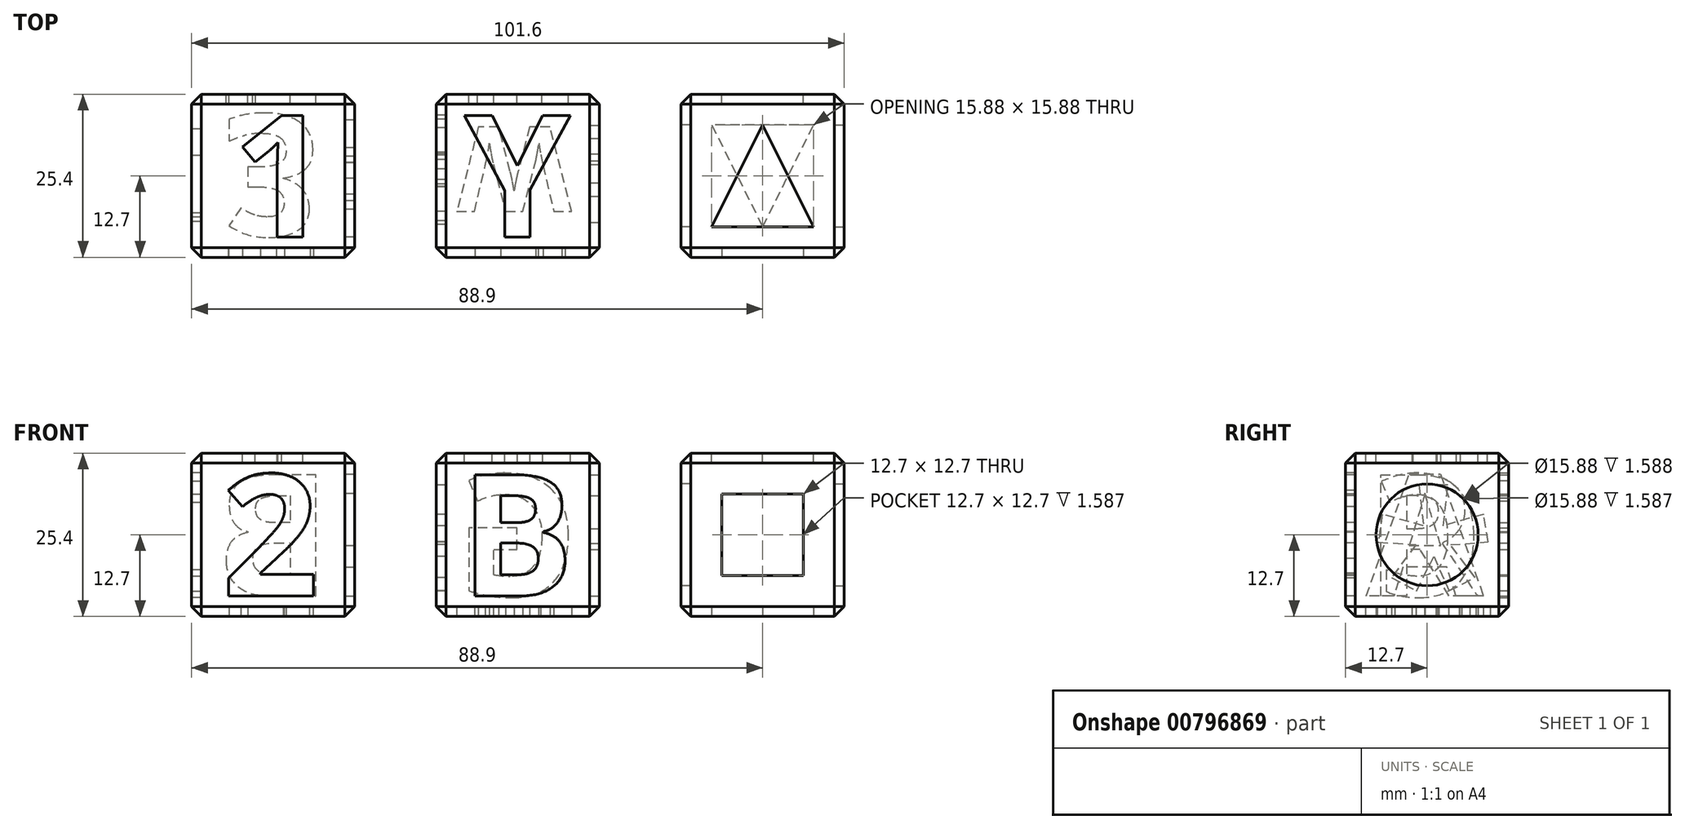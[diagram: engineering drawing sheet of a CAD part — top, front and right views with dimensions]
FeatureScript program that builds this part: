
annotation { "Feature Type Name" : "Feature", "Feature Type Description" : "" }
export const myFeature = defineFeature(function(context is Context, id is Id, definition is map)
    precondition{}
    {
        {
            var Q0;
            Q0=qCreatedBy(makeId("Top.planeOp"),FACE);
            var sketch = newSketch(context, id + "F0", { "sketchPlane" : qUnion([Q0])});
            skLineSegment(sketch, "E0.bottom", {"start": v(-12.7, 12.7) * mm, "end": v(12.7, 12.7) * mm});
            skLineSegment(sketch, "E0.top", {"start": v(-12.7, -12.7) * mm, "end": v(12.7, -12.7) * mm});
            skLineSegment(sketch, "E0.left", {"start": v(-12.7, 12.7) * mm, "end": v(-12.7, -12.7) * mm});
            skLineSegment(sketch, "E0.right", {"start": v(12.7, 12.7) * mm, "end": v(12.7, -12.7) * mm});
            skLineSegment(sketch, "E1.bottom", {"start": v(-50.8, 12.7) * mm, "end": v(-25.4, 12.7) * mm});
            skLineSegment(sketch, "E1.top", {"start": v(-50.8, -12.7) * mm, "end": v(-25.4, -12.7) * mm});
            skLineSegment(sketch, "E1.left", {"start": v(-50.8, 12.7) * mm, "end": v(-50.8, -12.7) * mm});
            skLineSegment(sketch, "E1.right", {"start": v(-25.4, 12.7) * mm, "end": v(-25.4, -12.7) * mm});
            skLineSegment(sketch, "E2.bottom", {"start": v(25.4, 12.7) * mm, "end": v(50.8, 12.7) * mm});
            skLineSegment(sketch, "E2.top", {"start": v(25.4, -12.7) * mm, "end": v(50.8, -12.7) * mm});
            skLineSegment(sketch, "E2.left", {"start": v(25.4, 12.7) * mm, "end": v(25.4, -12.7) * mm});
            skLineSegment(sketch, "E2.right", {"start": v(50.8, 12.7) * mm, "end": v(50.8, -12.7) * mm});
            skSolve(sketch);
        }
        {
            var Q0;
            Q0 = qSketchRegion(id + "F0", true);
            extrude(context, id + "F1", {"entities" : qUnion([Q0]), "depth" : 25.4 * mm, "offsetDistance" : 25.4 * mm});
        }
        {
            var Q0;
            Q0=makeQuery(id+"F1.opExtrude","CAP_FACE",FACE,{"disambiguationData":[OSD([sQuery(id+"F0.wireOp",EDGE,"E1.bottom"),sQuery(id+"F0.wireOp",EDGE,"E1.top"),sQuery(id+"F0.wireOp",EDGE,"E1.left"),sQuery(id+"F0.wireOp",EDGE,"E1.right")])],"isStart":false});
            var sketch = newSketch(context, id + "F2", { "sketchPlane" : qUnion([Q0])});
            skText(sketch, "E3", { "text": "1", "fontName": "OpenSans-Bold.ttf"});
            const initialGuessF2  = {"E3": [-0.04442, -0.00952, 1, 0, 0.01905]};
            skSetInitialGuess(sketch, initialGuessF2);
            skSolve(sketch);
        }
        {
            var Q0;
            Q0 = qSketchRegion(id + "F2", true);
            extrude(context, id + "F3", {"entities" : qUnion([Q0]), "operationType" : NewBodyOperationType.REMOVE, "oppositeDirection" : true, "depth" : 1.59 * mm, "offsetDistance" : 25.4 * mm});
        }
        {
            var Q0;
            Q0=makeQuery(id+"F1.opExtrude","SWEPT_FACE",FACE,{"disambiguationData":[OSD([sQuery(id+"F0.wireOp",EDGE,"E1.top")])]});
            var sketch = newSketch(context, id + "F4", { "sketchPlane" : qUnion([Q0])});
            skText(sketch, "E4", { "text": "2", "fontName": "OpenSans-Bold.ttf"});
            skPoint(sketch, "E4.firstSnap0", {"position": v(-38.1, 25.4) * mm});
            const initialGuessF4  = {"E4": [-0.04609, 0.00318, 1, 0, 0.01905]};
            skSetInitialGuess(sketch, initialGuessF4);
            skSolve(sketch);
        }
        {
            var Q0;
            Q0=makeQuery(id+"F4.imprint","IMPRINT",FACE,{"disambiguationData":[TD([[makeQuery(id+"F4.imprint","IMPRINT",EDGE,{"derivedFrom":sQuery(id+"F4.wireOp",EDGE,"E4.sketch_text.stroke-0")}),-1.0]])]});
            extrude(context, id + "F5", {"entities" : qUnion([Q0]), "operationType" : NewBodyOperationType.REMOVE, "oppositeDirection" : true, "depth" : 1.59 * mm, "offsetDistance" : 25.4 * mm});
        }
        {
            var Q0;
            Q0=makeQuery(id+"F1.opExtrude","CAP_FACE",FACE,{"disambiguationData":[OSD([sQuery(id+"F0.wireOp",EDGE,"E0.bottom"),sQuery(id+"F0.wireOp",EDGE,"E0.top"),sQuery(id+"F0.wireOp",EDGE,"E0.left"),sQuery(id+"F0.wireOp",EDGE,"E0.right")])],"isStart":false});
            var sketch = newSketch(context, id + "F6", { "sketchPlane" : qUnion([Q0])});
            skText(sketch, "E5", { "text": "Y", "fontName": "OpenSans-Bold.ttf"});
            const initialGuessF6  = {"E5": [-0.00835, -0.00953, 1, 0, 0.01905]};
            skSetInitialGuess(sketch, initialGuessF6);
            skSolve(sketch);
        }
        {
            var Q0;
            Q0=makeQuery(id+"F6.imprint","IMPRINT",FACE,{"disambiguationData":[TD([[makeQuery(id+"F6.imprint","IMPRINT",EDGE,{"derivedFrom":sQuery(id+"F6.wireOp",EDGE,"E5.sketch_text.stroke-0")}),-1.0]])]});
            extrude(context, id + "F7", {"entities" : qUnion([Q0]), "operationType" : NewBodyOperationType.REMOVE, "oppositeDirection" : true, "depth" : 1.59 * mm, "offsetDistance" : 25.4 * mm});
        }
        {
            var Q0;
            Q0=makeQuery(id+"F1.opExtrude","SWEPT_FACE",FACE,{"disambiguationData":[OSD([sQuery(id+"F0.wireOp",EDGE,"E0.top")])]});
            var sketch = newSketch(context, id + "F8", { "sketchPlane" : qUnion([Q0])});
            skText(sketch, "E6", { "text": "B", "fontName": "OpenSans-Bold.ttf"});
            const initialGuessF8  = {"E6": [-0.00905, 0.00318, 1, 0, 0.01905]};
            skSetInitialGuess(sketch, initialGuessF8);
            skSolve(sketch);
        }
        {
            var Q0;
            Q0 = qSketchRegion(id + "F8", true);
            extrude(context, id + "F9", {"entities" : qUnion([Q0]), "operationType" : NewBodyOperationType.REMOVE, "oppositeDirection" : true, "depth" : 1.59 * mm, "offsetDistance" : 25.4 * mm});
        }
        {
            var Q0;
            Q0=makeQuery(id+"F1.opExtrude","CAP_FACE",FACE,{"disambiguationData":[OSD([sQuery(id+"F0.wireOp",EDGE,"E0.bottom"),sQuery(id+"F0.wireOp",EDGE,"E0.top"),sQuery(id+"F0.wireOp",EDGE,"E0.left"),sQuery(id+"F0.wireOp",EDGE,"E0.right")])],"isStart":true});
            var sketch = newSketch(context, id + "F10", { "sketchPlane" : qUnion([Q0])});
            skText(sketch, "E7", { "text": "W", "fontName": "OpenSans-Bold.ttf"});
            const initialGuessF10  = {"E7": [-0.00952, -0.00762, 1, 0, 0.0133]};
            skSetInitialGuess(sketch, initialGuessF10);
            skSolve(sketch);
        }
        {
            var Q0;
            Q0 = qSketchRegion(id + "F10", true);
            extrude(context, id + "F11", {"entities" : qUnion([Q0]), "operationType" : NewBodyOperationType.REMOVE, "oppositeDirection" : true, "depth" : 1.59 * mm, "offsetDistance" : 25.4 * mm});
        }
        {
            var Q0;
            Q0=makeQuery(id+"F1.opExtrude","SWEPT_FACE",FACE,{"disambiguationData":[OSD([sQuery(id+"F0.wireOp",EDGE,"E0.bottom")])]});
            var sketch = newSketch(context, id + "F12", { "sketchPlane" : qUnion([Q0])});
            skText(sketch, "E8", { "text": "G", "fontName": "OpenSans-Bold.ttf"});
            const initialGuessF12  = {"E8": [-0.00938, 0.00317, 1, 0, 0.01905]};
            skSetInitialGuess(sketch, initialGuessF12);
            skSolve(sketch);
        }
        {
            var Q0;
            Q0 = qSketchRegion(id + "F12", true);
            extrude(context, id + "F13", {"entities" : qUnion([Q0]), "operationType" : NewBodyOperationType.REMOVE, "oppositeDirection" : true, "depth" : 1.59 * mm, "offsetDistance" : 25.4 * mm});
        }
        {
            var Q0;
            Q0=makeQuery(id+"F1.opExtrude","SWEPT_FACE",FACE,{"disambiguationData":[OSD([sQuery(id+"F0.wireOp",EDGE,"E0.right")])]});
            var sketch = newSketch(context, id + "F14", { "sketchPlane" : qUnion([Q0])});
            skText(sketch, "E9", { "text": "R", "fontName": "OpenSans-Bold.ttf"});
            const initialGuessF14  = {"E9": [-0.0096, 0.00317, 1, 0, 0.01905]};
            skSetInitialGuess(sketch, initialGuessF14);
            skSolve(sketch);
        }
        {
            var Q0;
            Q0 = qSketchRegion(id + "F14", true);
            extrude(context, id + "F15", {"entities" : qUnion([Q0]), "operationType" : NewBodyOperationType.REMOVE, "oppositeDirection" : true, "depth" : 1.59 * mm, "offsetDistance" : 25.4 * mm});
        }
        {
            var Q0;
            Q0=makeQuery(id+"F1.opExtrude","SWEPT_FACE",FACE,{"disambiguationData":[OSD([sQuery(id+"F0.wireOp",EDGE,"E0.left")])]});
            var sketch = newSketch(context, id + "F16", { "sketchPlane" : qUnion([Q0])});
            skText(sketch, "E10", { "text": "*", "fontName": "OpenSans-Bold.ttf"});
            const initialGuessF16  = {"E10": [-0.01056, -0.00635, 1, 0, 0.0254]};
            skSetInitialGuess(sketch, initialGuessF16);
            skSolve(sketch);
        }
        {
            var Q0;
            Q0 = qSketchRegion(id + "F16", true);
            extrude(context, id + "F17", {"entities" : qUnion([Q0]), "operationType" : NewBodyOperationType.REMOVE, "oppositeDirection" : true, "depth" : 1.59 * mm, "offsetDistance" : 25.4 * mm});
        }
        {
            var Q0;
            Q0=makeQuery(id+"F1.opExtrude","CAP_FACE",FACE,{"disambiguationData":[OSD([sQuery(id+"F0.wireOp",EDGE,"E1.bottom"),sQuery(id+"F0.wireOp",EDGE,"E1.top"),sQuery(id+"F0.wireOp",EDGE,"E1.left"),sQuery(id+"F0.wireOp",EDGE,"E1.right")])],"isStart":true});
            var sketch = newSketch(context, id + "F18", { "sketchPlane" : qUnion([Q0])});
            skText(sketch, "E11", { "text": "3", "fontName": "OpenSans-Bold.ttf"});
            const initialGuessF18  = {"E11": [-0.046, -0.00953, 1, 0, 0.01905]};
            skSetInitialGuess(sketch, initialGuessF18);
            skSolve(sketch);
        }
        {
            var Q0;
            Q0 = qSketchRegion(id + "F18", true);
            extrude(context, id + "F19", {"entities" : qUnion([Q0]), "operationType" : NewBodyOperationType.REMOVE, "oppositeDirection" : true, "depth" : 1.59 * mm, "offsetDistance" : 25.4 * mm});
        }
        {
            var Q0;
            Q0=makeQuery(id+"F1.opExtrude","SWEPT_FACE",FACE,{"disambiguationData":[OSD([sQuery(id+"F0.wireOp",EDGE,"E1.right")])]});
            var sketch = newSketch(context, id + "F20", { "sketchPlane" : qUnion([Q0])});
            skText(sketch, "E12", { "text": "A", "fontName": "OpenSans-Bold.ttf"});
            const initialGuessF20  = {"E12": [-0.00948, 0.00318, 1, 0, 0.01905]};
            skSetInitialGuess(sketch, initialGuessF20);
            skSolve(sketch);
        }
        {
            var Q0;
            Q0 = qSketchRegion(id + "F20", true);
            extrude(context, id + "F21", {"entities" : qUnion([Q0]), "operationType" : NewBodyOperationType.REMOVE, "oppositeDirection" : true, "depth" : 1.59 * mm, "offsetDistance" : 25.4 * mm});
        }
        {
            var Q0;
            Q0=makeQuery(id+"F1.opExtrude","SWEPT_FACE",FACE,{"disambiguationData":[OSD([sQuery(id+"F0.wireOp",EDGE,"E1.bottom")])]});
            var sketch = newSketch(context, id + "F22", { "sketchPlane" : qUnion([Q0])});
            skText(sketch, "E13", { "text": "B\n", "fontName": "OpenSans-Bold.ttf"});
            const initialGuessF22  = {"E13": [0.02905, 0.00318, 1, 0, 0.01905]};
            skSetInitialGuess(sketch, initialGuessF22);
            skSolve(sketch);
        }
        {
            var Q0;
            Q0 = qSketchRegion(id + "F22", true);
            extrude(context, id + "F23", {"entities" : qUnion([Q0]), "operationType" : NewBodyOperationType.REMOVE, "oppositeDirection" : true, "depth" : 1.59 * mm, "offsetDistance" : 25.4 * mm});
        }
        {
            var Q0;
            Q0=makeQuery(id+"F1.opExtrude","SWEPT_FACE",FACE,{"disambiguationData":[OSD([sQuery(id+"F0.wireOp",EDGE,"E1.left")])]});
            var sketch = newSketch(context, id + "F24", { "sketchPlane" : qUnion([Q0])});
            skText(sketch, "E14", { "text": "C", "fontName": "OpenSans-Bold.ttf"});
            const initialGuessF24  = {"E14": [-0.00882, 0.00318, 1, 0, 0.01905]};
            skSetInitialGuess(sketch, initialGuessF24);
            skSolve(sketch);
        }
        {
            var Q0;
            Q0 = qSketchRegion(id + "F24", true);
            extrude(context, id + "F25", {"entities" : qUnion([Q0]), "operationType" : NewBodyOperationType.REMOVE, "oppositeDirection" : true, "depth" : 1.59 * mm, "offsetDistance" : 25.4 * mm});
        }
        {
            var Q0;
            Q0=makeQuery(id+"F1.opExtrude","CAP_FACE",FACE,{"disambiguationData":[OSD([sQuery(id+"F0.wireOp",EDGE,"E2.bottom"),sQuery(id+"F0.wireOp",EDGE,"E2.top"),sQuery(id+"F0.wireOp",EDGE,"E2.left"),sQuery(id+"F0.wireOp",EDGE,"E2.right")])],"isStart":false});
            var sketch = newSketch(context, id + "F26", { "sketchPlane" : qUnion([Q0])});
            skLineSegment(sketch, "E15", {"start": v(30.16, -7.94) * mm, "end": v(38.1, 7.94) * mm});
            skLineSegment(sketch, "E16", {"start": v(38.1, 7.94) * mm, "end": v(46.04, -7.94) * mm});
            skLineSegment(sketch, "E17", {"start": v(46.04, -7.94) * mm, "end": v(30.16, -7.94) * mm});
            skSolve(sketch);
        }
        {
            var Q0;
            Q0 = qSketchRegion(id + "F26", true);
            extrude(context, id + "F27", {"entities" : qUnion([Q0]), "operationType" : NewBodyOperationType.REMOVE, "oppositeDirection" : true, "depth" : 1.59 * mm, "offsetDistance" : 25.4 * mm});
        }
        {
            var Q0;
            Q0=makeQuery(id+"F1.opExtrude","CAP_FACE",FACE,{"disambiguationData":[OSD([sQuery(id+"F0.wireOp",EDGE,"E2.bottom"),sQuery(id+"F0.wireOp",EDGE,"E2.top"),sQuery(id+"F0.wireOp",EDGE,"E2.left"),sQuery(id+"F0.wireOp",EDGE,"E2.right")])],"isStart":true});
            var sketch = newSketch(context, id + "F28", { "sketchPlane" : qUnion([Q0])});
            skLineSegment(sketch, "E18", {"start": v(30.16, -7.94) * mm, "end": v(38.1, 7.94) * mm});
            skLineSegment(sketch, "E19", {"start": v(38.1, 7.94) * mm, "end": v(46.04, -7.94) * mm});
            skLineSegment(sketch, "E20", {"start": v(46.04, -7.94) * mm, "end": v(30.16, -7.94) * mm});
            skSolve(sketch);
        }
        {
            var Q0;
            Q0 = qSketchRegion(id + "F28", true);
            extrude(context, id + "F29", {"entities" : qUnion([Q0]), "operationType" : NewBodyOperationType.REMOVE, "oppositeDirection" : true, "depth" : 1.59 * mm, "offsetDistance" : 25.4 * mm});
        }
        {
            var Q0;
            Q0=makeQuery(id+"F1.opExtrude","SWEPT_FACE",FACE,{"disambiguationData":[OSD([sQuery(id+"F0.wireOp",EDGE,"E2.bottom")])]});
            var sketch = newSketch(context, id + "F30", { "sketchPlane" : qUnion([Q0])});
            skLineSegment(sketch, "E21.bottom", {"start": v(-44.45, 19.05) * mm, "end": v(-31.75, 19.05) * mm});
            skLineSegment(sketch, "E21.top", {"start": v(-44.45, 6.35) * mm, "end": v(-31.75, 6.35) * mm});
            skLineSegment(sketch, "E21.left", {"start": v(-44.45, 19.05) * mm, "end": v(-44.45, 6.35) * mm});
            skLineSegment(sketch, "E21.right", {"start": v(-31.75, 19.05) * mm, "end": v(-31.75, 6.35) * mm});
            skSolve(sketch);
        }
        {
            var Q0;
            Q0=makeQuery(id+"F30.imprint","IMPRINT",FACE,{"disambiguationData":[TD([[makeQuery(id+"F30.imprint","IMPRINT",EDGE,{"derivedFrom":sQuery(id+"F30.wireOp",EDGE,"E21.bottom")}),-1.0]])]});
            extrude(context, id + "F31", {"entities" : qUnion([Q0]), "operationType" : NewBodyOperationType.REMOVE, "oppositeDirection" : true, "depth" : 1.59 * mm, "offsetDistance" : 25.4 * mm});
        }
        {
            var Q0;
            Q0=makeQuery(id+"F1.opExtrude","SWEPT_FACE",FACE,{"disambiguationData":[OSD([sQuery(id+"F0.wireOp",EDGE,"E2.top")])]});
            var sketch = newSketch(context, id + "F32", { "sketchPlane" : qUnion([Q0])});
            skLineSegment(sketch, "E22.bottom", {"start": v(31.75, 19.05) * mm, "end": v(44.45, 19.05) * mm});
            skLineSegment(sketch, "E22.top", {"start": v(31.75, 6.35) * mm, "end": v(44.45, 6.35) * mm});
            skLineSegment(sketch, "E22.left", {"start": v(31.75, 19.05) * mm, "end": v(31.75, 6.35) * mm});
            skLineSegment(sketch, "E22.right", {"start": v(44.45, 19.05) * mm, "end": v(44.45, 6.35) * mm});
            skSolve(sketch);
        }
        {
            var Q0;
            Q0 = qSketchRegion(id + "F32", true);
            extrude(context, id + "F33", {"entities" : qUnion([Q0]), "operationType" : NewBodyOperationType.REMOVE, "oppositeDirection" : true, "depth" : 1.59 * mm, "offsetDistance" : 25.4 * mm});
        }
        {
            var Q0;
            Q0=makeQuery(id+"F1.opExtrude","SWEPT_FACE",FACE,{"disambiguationData":[OSD([sQuery(id+"F0.wireOp",EDGE,"E2.left")])]});
            var sketch = newSketch(context, id + "F34", { "sketchPlane" : qUnion([Q0])});
            skCircle(sketch, "E23", {"center": v(0, 12.7) * mm, "radius": 7.94 * mm});
            skSolve(sketch);
        }
        {
            var Q0;
            Q0 = qSketchRegion(id + "F34", true);
            extrude(context, id + "F35", {"entities" : qUnion([Q0]), "operationType" : NewBodyOperationType.REMOVE, "oppositeDirection" : true, "depth" : 1.59 * mm, "offsetDistance" : 25.4 * mm});
        }
        {
            var Q0;
            Q0=makeQuery(id+"F1.opExtrude","SWEPT_FACE",FACE,{"disambiguationData":[OSD([sQuery(id+"F0.wireOp",EDGE,"E2.right")])]});
            var sketch = newSketch(context, id + "F36", { "sketchPlane" : qUnion([Q0])});
            skCircle(sketch, "E24", {"center": v(0, 12.7) * mm, "radius": 7.94 * mm});
            skSolve(sketch);
        }
        {
            var Q0;
            Q0 = qSketchRegion(id + "F36", true);
            extrude(context, id + "F37", {"entities" : qUnion([Q0]), "operationType" : NewBodyOperationType.REMOVE, "oppositeDirection" : true, "depth" : 1.59 * mm, "offsetDistance" : 25.4 * mm});
        }
        {
            var Q0;
            Q0=makeQuery(id+"F1.opExtrude","SWEPT_EDGE",EDGE,{"disambiguationData":[OSD([sQuery(id+"F0.wireOp",EDGE,"E2.top"),sQuery(id+"F0.wireOp",EDGE,"E2.right")])]});
            var Q1;
            Q1=makeQuery(id+"F1.opExtrude","CAP_EDGE",EDGE,{"disambiguationData":[OSD([sQuery(id+"F0.wireOp",EDGE,"E2.right")])],"isStart":false});
            var Q2;
            Q2=makeQuery(id+"F1.opExtrude","CAP_EDGE",EDGE,{"disambiguationData":[OSD([sQuery(id+"F0.wireOp",EDGE,"E2.right")])],"isStart":true});
            var Q3;
            Q3=makeQuery(id+"F1.opExtrude","SWEPT_EDGE",EDGE,{"disambiguationData":[OSD([sQuery(id+"F0.wireOp",EDGE,"E2.bottom"),sQuery(id+"F0.wireOp",EDGE,"E2.right")])]});
            var Q4;
            Q4=makeQuery(id+"F1.opExtrude","CAP_EDGE",EDGE,{"disambiguationData":[OSD([sQuery(id+"F0.wireOp",EDGE,"E2.top")])],"isStart":true});
            var Q5;
            Q5=makeQuery(id+"F1.opExtrude","CAP_EDGE",EDGE,{"disambiguationData":[OSD([sQuery(id+"F0.wireOp",EDGE,"E2.bottom")])],"isStart":true});
            var Q6;
            Q6=makeQuery(id+"F1.opExtrude","CAP_EDGE",EDGE,{"disambiguationData":[OSD([sQuery(id+"F0.wireOp",EDGE,"E2.bottom")])],"isStart":false});
            var Q7;
            Q7=makeQuery(id+"F1.opExtrude","CAP_EDGE",EDGE,{"disambiguationData":[OSD([sQuery(id+"F0.wireOp",EDGE,"E2.top")])],"isStart":false});
            var Q8;
            Q8=makeQuery(id+"F1.opExtrude","CAP_EDGE",EDGE,{"disambiguationData":[OSD([sQuery(id+"F0.wireOp",EDGE,"E2.left")])],"isStart":false});
            var Q9;
            Q9=makeQuery(id+"F1.opExtrude","SWEPT_EDGE",EDGE,{"disambiguationData":[OSD([sQuery(id+"F0.wireOp",EDGE,"E2.top"),sQuery(id+"F0.wireOp",EDGE,"E2.left")])]});
            var Q10;
            Q10=makeQuery(id+"F1.opExtrude","CAP_EDGE",EDGE,{"disambiguationData":[OSD([sQuery(id+"F0.wireOp",EDGE,"E2.left")])],"isStart":true});
            var Q11;
            Q11=makeQuery(id+"F1.opExtrude","SWEPT_EDGE",EDGE,{"disambiguationData":[OSD([sQuery(id+"F0.wireOp",EDGE,"E2.bottom"),sQuery(id+"F0.wireOp",EDGE,"E2.left")])]});
            chamfer(context, id + "F38", {"entities" : qUnion([Q0, Q1, Q2, Q3, Q4, Q5, Q6, Q7, Q8, Q9, Q10, Q11]), "width" : 1.52 * mm, "tangentPropagation" : true});
        }
        {
            var Q0;
            Q0=makeQuery(id+"F1.opExtrude","SWEPT_EDGE",EDGE,{"disambiguationData":[OSD([sQuery(id+"F0.wireOp",EDGE,"E1.bottom"),sQuery(id+"F0.wireOp",EDGE,"E1.left")])]});
            var Q1;
            Q1=makeQuery(id+"F1.opExtrude","CAP_EDGE",EDGE,{"disambiguationData":[OSD([sQuery(id+"F0.wireOp",EDGE,"E1.left")])],"isStart":true});
            var Q2;
            Q2=makeQuery(id+"F1.opExtrude","CAP_EDGE",EDGE,{"disambiguationData":[OSD([sQuery(id+"F0.wireOp",EDGE,"E1.left")])],"isStart":false});
            var Q3;
            Q3=makeQuery(id+"F1.opExtrude","SWEPT_EDGE",EDGE,{"disambiguationData":[OSD([sQuery(id+"F0.wireOp",EDGE,"E1.top"),sQuery(id+"F0.wireOp",EDGE,"E1.left")])]});
            var Q4;
            Q4=makeQuery(id+"F1.opExtrude","CAP_EDGE",EDGE,{"disambiguationData":[OSD([sQuery(id+"F0.wireOp",EDGE,"E1.top")])],"isStart":false});
            var Q5;
            Q5=makeQuery(id+"F1.opExtrude","CAP_EDGE",EDGE,{"disambiguationData":[OSD([sQuery(id+"F0.wireOp",EDGE,"E1.top")])],"isStart":true});
            var Q6;
            Q6=makeQuery(id+"F1.opExtrude","SWEPT_EDGE",EDGE,{"disambiguationData":[OSD([sQuery(id+"F0.wireOp",EDGE,"E1.top"),sQuery(id+"F0.wireOp",EDGE,"E1.right")])]});
            var Q7;
            Q7=makeQuery(id+"F1.opExtrude","CAP_EDGE",EDGE,{"disambiguationData":[OSD([sQuery(id+"F0.wireOp",EDGE,"E1.right")])],"isStart":false});
            var Q8;
            Q8=makeQuery(id+"F1.opExtrude","CAP_EDGE",EDGE,{"disambiguationData":[OSD([sQuery(id+"F0.wireOp",EDGE,"E0.bottom")])],"isStart":false});
            var Q9;
            Q9=makeQuery(id+"F1.opExtrude","CAP_EDGE",EDGE,{"disambiguationData":[OSD([sQuery(id+"F0.wireOp",EDGE,"E1.bottom")])],"isStart":false});
            var Q10;
            Q10=makeQuery(id+"F1.opExtrude","SWEPT_EDGE",EDGE,{"disambiguationData":[OSD([sQuery(id+"F0.wireOp",EDGE,"E0.bottom"),sQuery(id+"F0.wireOp",EDGE,"E0.left")])]});
            var Q11;
            Q11=makeQuery(id+"F1.opExtrude","CAP_EDGE",EDGE,{"disambiguationData":[OSD([sQuery(id+"F0.wireOp",EDGE,"E0.left")])],"isStart":true});
            var Q12;
            Q12=makeQuery(id+"F1.opExtrude","SWEPT_EDGE",EDGE,{"disambiguationData":[OSD([sQuery(id+"F0.wireOp",EDGE,"E0.top"),sQuery(id+"F0.wireOp",EDGE,"E0.left")])]});
            var Q13;
            Q13=makeQuery(id+"F1.opExtrude","CAP_EDGE",EDGE,{"disambiguationData":[OSD([sQuery(id+"F0.wireOp",EDGE,"E0.top")])],"isStart":false});
            var Q14;
            Q14=makeQuery(id+"F1.opExtrude","CAP_EDGE",EDGE,{"disambiguationData":[OSD([sQuery(id+"F0.wireOp",EDGE,"E0.left")])],"isStart":false});
            var Q15;
            Q15=makeQuery(id+"F1.opExtrude","CAP_EDGE",EDGE,{"disambiguationData":[OSD([sQuery(id+"F0.wireOp",EDGE,"E0.top")])],"isStart":true});
            var Q16;
            Q16=makeQuery(id+"F1.opExtrude","SWEPT_EDGE",EDGE,{"disambiguationData":[OSD([sQuery(id+"F0.wireOp",EDGE,"E0.top"),sQuery(id+"F0.wireOp",EDGE,"E0.right")])]});
            var Q17;
            Q17=makeQuery(id+"F1.opExtrude","CAP_EDGE",EDGE,{"disambiguationData":[OSD([sQuery(id+"F0.wireOp",EDGE,"E0.right")])],"isStart":false});
            var Q18;
            Q18=makeQuery(id+"F1.opExtrude","CAP_EDGE",EDGE,{"disambiguationData":[OSD([sQuery(id+"F0.wireOp",EDGE,"E1.bottom")])],"isStart":true});
            var Q19;
            Q19=makeQuery(id+"F1.opExtrude","CAP_EDGE",EDGE,{"disambiguationData":[OSD([sQuery(id+"F0.wireOp",EDGE,"E1.right")])],"isStart":true});
            var Q20;
            Q20=makeQuery(id+"F1.opExtrude","SWEPT_EDGE",EDGE,{"disambiguationData":[OSD([sQuery(id+"F0.wireOp",EDGE,"E1.bottom"),sQuery(id+"F0.wireOp",EDGE,"E1.right")])]});
            var Q21;
            Q21=makeQuery(id+"F1.opExtrude","CAP_EDGE",EDGE,{"disambiguationData":[OSD([sQuery(id+"F0.wireOp",EDGE,"E0.bottom")])],"isStart":true});
            var Q22;
            Q22=makeQuery(id+"F1.opExtrude","SWEPT_EDGE",EDGE,{"disambiguationData":[OSD([sQuery(id+"F0.wireOp",EDGE,"E0.bottom"),sQuery(id+"F0.wireOp",EDGE,"E0.right")])]});
            var Q23;
            Q23=makeQuery(id+"F1.opExtrude","CAP_EDGE",EDGE,{"disambiguationData":[OSD([sQuery(id+"F0.wireOp",EDGE,"E0.right")])],"isStart":true});
            chamfer(context, id + "F39", {"entities" : qUnion([Q0, Q1, Q2, Q3, Q4, Q5, Q6, Q7, Q8, Q9, Q10, Q11, Q12, Q13, Q14, Q15, Q16, Q17, Q18, Q19, Q20, Q21, Q22, Q23]), "width" : 1.52 * mm, "tangentPropagation" : true});
        }
    });
